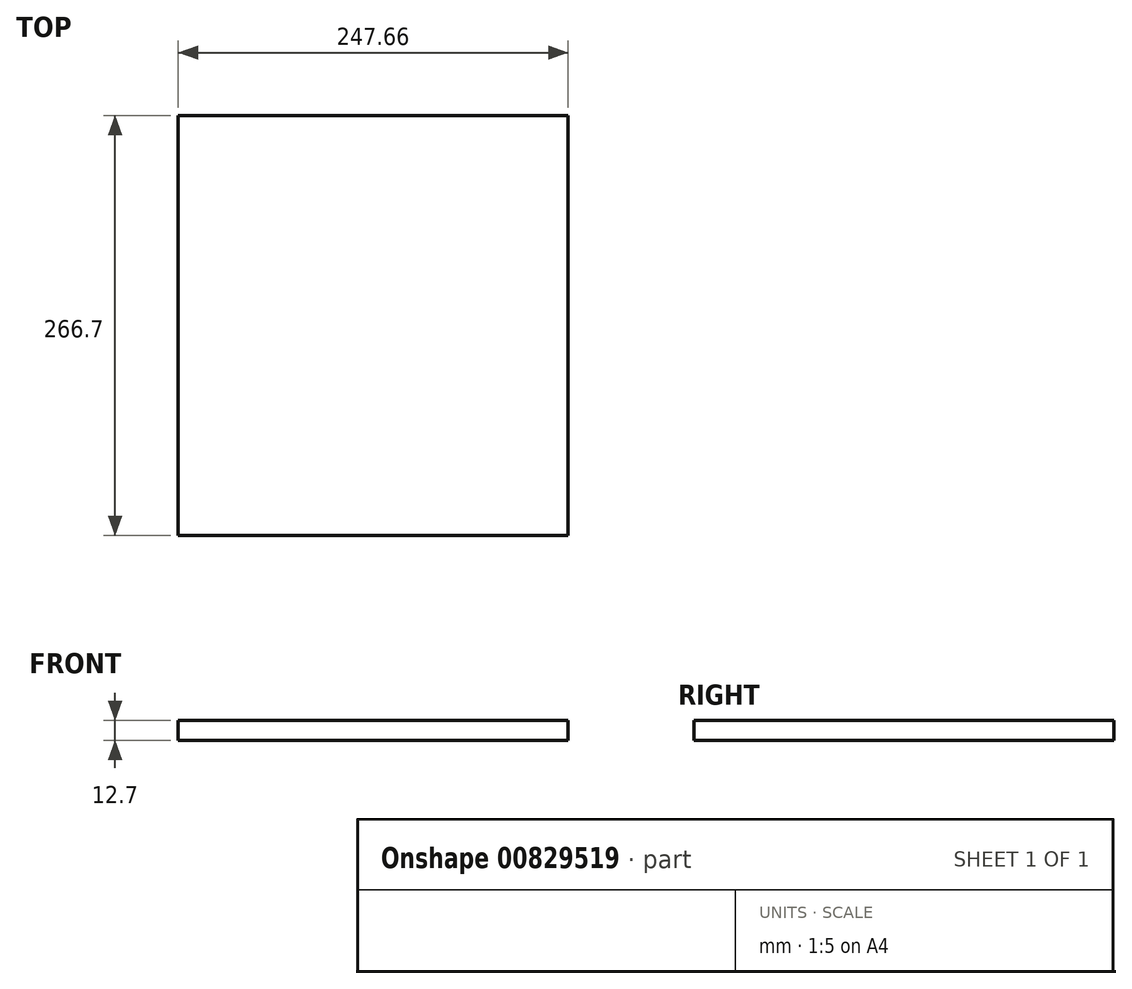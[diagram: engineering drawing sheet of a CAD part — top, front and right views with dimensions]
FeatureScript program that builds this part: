
annotation { "Feature Type Name" : "Feature", "Feature Type Description" : "" }
export const myFeature = defineFeature(function(context is Context, id is Id, definition is map)
    precondition{}
    {
        {
            var Q0;
            Q0=qCreatedBy(makeId("Top.planeOp"),FACE);
            var sketch = newSketch(context, id + "F0", { "sketchPlane" : qUnion([Q0])});
            skLineSegment(sketch, "E0.bottom", {"start": v(-123.83, -133.35) * mm, "end": v(123.83, -133.35) * mm});
            skLineSegment(sketch, "E0.top", {"start": v(-123.83, 133.35) * mm, "end": v(123.83, 133.35) * mm});
            skLineSegment(sketch, "E0.left", {"start": v(-123.83, -133.35) * mm, "end": v(-123.83, 133.35) * mm});
            skLineSegment(sketch, "E0.right", {"start": v(123.83, -133.35) * mm, "end": v(123.83, 133.35) * mm});
            skPoint(sketch, "E0.middle", {"position": v(0, 0) * mm});
            skSolve(sketch);
        }
        {
            var Q0;
            Q0 = qSketchRegion(id + "F0", true);
            extrude(context, id + "F1", {"entities" : qUnion([Q0]), "depth" : 12.7 * mm, "offsetDistance" : 25.4 * mm});
        }
    });
